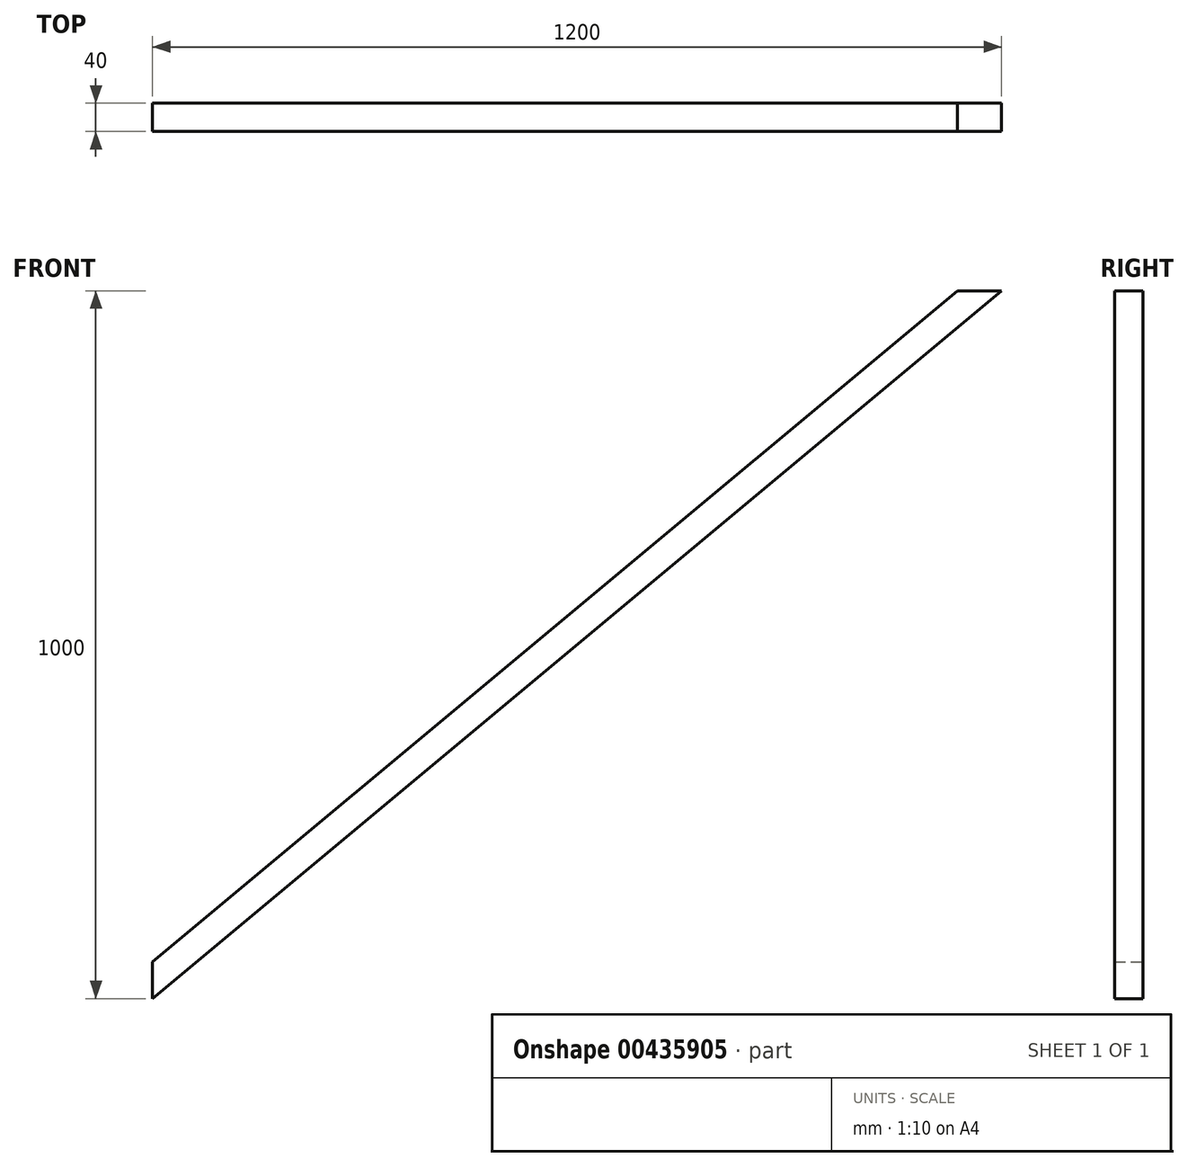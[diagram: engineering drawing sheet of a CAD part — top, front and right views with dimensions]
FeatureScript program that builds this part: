
annotation { "Feature Type Name" : "Feature", "Feature Type Description" : "" }
export const myFeature = defineFeature(function(context is Context, id is Id, definition is map)
    precondition{}
    {
        {
            var Q0;
            Q0=qCreatedBy(makeId("Front.planeOp"),FACE);
            var sketch = newSketch(context, id + "F0", { "sketchPlane" : qUnion([Q0])});
            skLineSegment(sketch, "E0", {"start": v(0, -1000) * mm, "end": v(1200, 0) * mm});
            skLineSegment(sketch, "E1", {"start": v(1137.7, 0) * mm, "end": v(1200, 0) * mm});
            skLineSegment(sketch, "E2", {"start": v(1137.7, 0) * mm, "end": v(0, -948.09) * mm});
            skLineSegment(sketch, "E3", {"start": v(0, -948.09) * mm, "end": v(0, -1000) * mm});
            skSolve(sketch);
        }
        {
            var Q0;
            Q0 = qSketchRegion(id + "F0", true);
            extrude(context, id + "F1", {"entities" : qUnion([Q0]), "depth" : 40 * mm});
        }
    });
